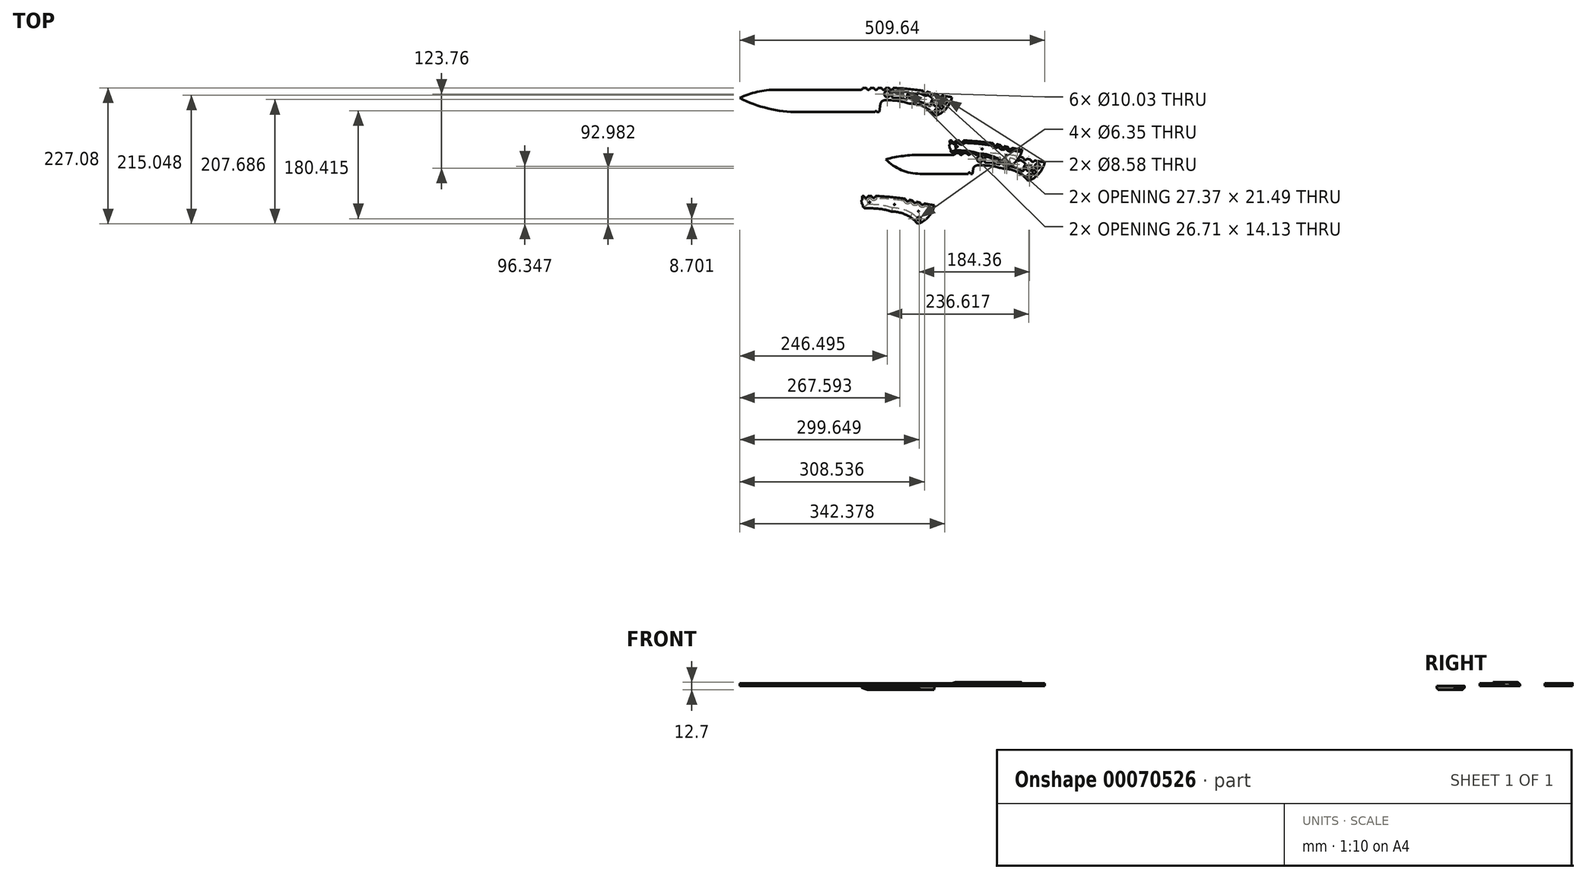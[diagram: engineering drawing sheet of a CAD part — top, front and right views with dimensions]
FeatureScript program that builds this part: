
annotation { "Feature Type Name" : "Feature", "Feature Type Description" : "" }
export const myFeature = defineFeature(function(context is Context, id is Id, definition is map)
    precondition{}
    {
        {
            var Q0;
            Q0=qCreatedBy(makeId("Top.planeOp"),FACE);
            var sketch = newSketch(context, id + "F0", { "sketchPlane" : qUnion([Q0])});
            skLineSegment(sketch, "E0", {"start": v(-84.54, 13.28) * mm, "end": v(-84.54, 13.28) * mm});
            skPoint(sketch, "E1", {"position": v(108.15, 3.1) * mm});
            skLineSegment(sketch, "E2", {"start": v(-12.95, 49.77) * mm, "end": v(-6.6, 49.77) * mm});
            skLineSegment(sketch, "E3", {"start": v(-0.25, 49.77) * mm, "end": v(6.1, 49.77) * mm});
            skLineSegment(sketch, "E4", {"start": v(-41.06, 46.66) * mm, "end": v(-70.9, 46.66) * mm});
            skPoint(sketch, "E5", {"position": v(-130.65, 40.32) * mm});
            skPoint(sketch, "E6", {"position": v(-84.54, 13.28) * mm});
            skLineSegment(sketch, "E7", {"start": v(15.4, 14.9) * mm, "end": v(-72, 14.9) * mm});
            skLineSegment(sketch, "E8", {"start": v(-41.06, 46.66) * mm, "end": v(-16.12, 46.66) * mm});
            skLineSegment(sketch, "E9", {"start": v(31.12, 29.1) * mm, "end": v(24.2, 29.1) * mm});
            skLineSegment(sketch, "E10", {"start": v(15.4, 14.9) * mm, "end": v(16.47, 23.28) * mm});
            skArc(sketch, "E11", {"start": v(24.2, 29.1) * mm, "mid": v(19.36, 27.48) * mm, "end": v(16.47, 23.28) * mm});
            skPoint(sketch, "E12", {"position": v(95.42, 14.98) * mm});
            skPoint(sketch, "E13", {"position": v(96.98, 42.66) * mm});
            skPoint(sketch, "E14", {"position": v(136.23, 34.28) * mm});
            skArc(sketch, "E15", {"start": v(83.35, 45.62) * mm, "mid": v(60.26, 48.23) * mm, "end": v(37.06, 49.73) * mm});
            skArc(sketch, "E16", {"start": v(96.98, 42.66) * mm, "mid": v(90.2, 44.33) * mm, "end": v(83.35, 45.62) * mm});
            skArc(sketch, "E17", {"start": v(96.98, 42.66) * mm, "mid": v(116.43, 37.68) * mm, "end": v(136.23, 34.28) * mm});
            skArc(sketch, "E18", {"start": v(64.66, 23.87) * mm, "mid": v(48.1, 27.78) * mm, "end": v(31.12, 29.1) * mm});
            skArc(sketch, "E19", {"start": v(108.15, 3.1) * mm, "mid": v(126.27, 15.01) * mm, "end": v(136.23, 34.28) * mm});
            skPoint(sketch, "E20", {"position": v(109.7, 24.2) * mm});
            skPoint(sketch, "E21", {"position": v(27.97, 39.43) * mm});
            skPoint(sketch, "E22", {"position": v(69.43, 35.5) * mm});
            skCircle(sketch, "E23", {"center": v(27.97, 39.43) * mm, "radius": 5.02 * mm});
            skCircle(sketch, "E24", {"center": v(69.43, 35.5) * mm, "radius": 5.02 * mm});
            skCircle(sketch, "E25", {"center": v(109.7, 24.2) * mm, "radius": 5.02 * mm});
            skLineSegment(sketch, "E26", {"start": v(49.3, 44.08) * mm, "end": v(39.93, 44.8) * mm});
            skPoint(sketch, "E27", {"position": v(38.2, 44.27) * mm});
            skPoint(sketch, "E28", {"position": v(36.72, 43.37) * mm});
            skPoint(sketch, "E29", {"position": v(36.71, 43.38) * mm});
            skPoint(sketch, "E30", {"position": v(36.14, 42.04) * mm});
            skLineSegment(sketch, "E31", {"start": v(60.01, 30.7) * mm, "end": v(48.1, 32.86) * mm});
            skLineSegment(sketch, "E32", {"start": v(49.3, 44.08) * mm, "end": v(61.08, 42.46) * mm});
            skArc(sketch, "E33", {"start": v(62.23, 40.16) * mm, "mid": v(62.26, 41.61) * mm, "end": v(61.08, 42.46) * mm});
            skArc(sketch, "E34", {"start": v(60.01, 30.7) * mm, "mid": v(61.2, 31.1) * mm, "end": v(61.46, 32.34) * mm});
            skPoint(sketch, "E35", {"position": v(101.38, 22.16) * mm});
            skArc(sketch, "E36", {"start": v(97.9, 19.97) * mm, "mid": v(88.55, 24.54) * mm, "end": v(78.52, 27.36) * mm});
            skArc(sketch, "E37", {"start": v(97.9, 19.97) * mm, "mid": v(100.33, 19.98) * mm, "end": v(101.38, 22.16) * mm});
            skArc(sketch, "E38", {"start": v(86.88, 38.6) * mm, "mid": v(83.15, 40.14) * mm, "end": v(79.22, 41.06) * mm});
            skArc(sketch, "E39", {"start": v(79.22, 41.06) * mm, "mid": v(77.66, 40.69) * mm, "end": v(77.18, 39.16) * mm});
            skArc(sketch, "E40", {"start": v(98.36, 36.23) * mm, "mid": v(96.56, 37.18) * mm, "end": v(94.53, 37.33) * mm});
            skArc(sketch, "E41", {"start": v(102.92, 29.44) * mm, "mid": v(103.7, 31.05) * mm, "end": v(102.92, 32.65) * mm});
            skArc(sketch, "E42", {"start": v(102.92, 29.44) * mm, "mid": v(101.33, 25.97) * mm, "end": v(101.38, 22.16) * mm});
            skArc(sketch, "E43", {"start": v(35.72, 35.78) * mm, "mid": v(36.45, 38.52) * mm, "end": v(36.31, 41.35) * mm});
            skArc(sketch, "E44", {"start": v(35.72, 35.78) * mm, "mid": v(36.05, 34.52) * mm, "end": v(37.13, 33.78) * mm});
            skLineSegment(sketch, "E45", {"start": v(37.13, 33.78) * mm, "end": v(48.1, 32.86) * mm});
            skArc(sketch, "E46", {"start": v(95.42, 14.98) * mm, "mid": v(80.62, 21.43) * mm, "end": v(64.66, 23.87) * mm});
            skArc(sketch, "E47", {"start": v(108.15, 3.1) * mm, "mid": v(102.33, 9.63) * mm, "end": v(95.42, 14.98) * mm});
            skLineSegment(sketch, "E48", {"start": v(108.15, 3.1) * mm, "end": v(108.15, 3.1) * mm});
            skArc(sketch, "E49", {"start": v(86.88, 38.6) * mm, "mid": v(90.58, 37.18) * mm, "end": v(94.53, 37.33) * mm});
            skLineSegment(sketch, "E50", {"start": v(98.36, 36.23) * mm, "end": v(102.92, 32.65) * mm});
            skArc(sketch, "E51", {"start": v(39.93, 44.8) * mm, "mid": v(37.35, 43.88) * mm, "end": v(36.31, 41.35) * mm});
            skArc(sketch, "E52", {"start": v(62.23, 40.16) * mm, "mid": v(61.06, 36.33) * mm, "end": v(61.46, 32.34) * mm});
            skArc(sketch, "E53", {"start": v(76.66, 31.15) * mm, "mid": v(76.58, 28.76) * mm, "end": v(78.52, 27.36) * mm});
            skArc(sketch, "E54", {"start": v(76.66, 31.15) * mm, "mid": v(77.84, 35.1) * mm, "end": v(77.18, 39.16) * mm});
            skCircle(sketch, "E55", {"center": v(123.85, 27.57) * mm, "radius": 4.3 * mm});
            skCircle(sketch, "E56", {"center": v(110.6, 11.8) * mm, "radius": 3.18 * mm});
            skCircle(sketch, "E57", {"center": v(118.5, 17.8) * mm, "radius": 2.9 * mm});
            skCircle(sketch, "E58", {"center": v(10.19, 14.9) * mm, "radius": 2.06 * mm});
            skArc(sketch, "E59", {"start": v(-129.4, 39) * mm, "mid": v(-103.12, 21.18) * mm, "end": v(-72, 14.9) * mm});
            skArc(sketch, "E60", {"start": v(-70.9, 46.66) * mm, "mid": v(-100.4, 44.74) * mm, "end": v(-129.4, 39) * mm});
            skArc(sketch, "E61", {"start": v(-16.12, 46.66) * mm, "mid": v(-13.9, 47.57) * mm, "end": v(-12.95, 49.77) * mm});
            skArc(sketch, "E62", {"start": v(-6.6, 49.77) * mm, "mid": v(-3.42, 46.58) * mm, "end": v(-0.25, 49.77) * mm});
            skArc(sketch, "E63", {"start": v(6.1, 49.77) * mm, "mid": v(9.28, 46.6) * mm, "end": v(12.45, 49.77) * mm});
            skLineSegment(sketch, "E64", {"start": v(12.45, 49.77) * mm, "end": v(18.8, 49.77) * mm});
            skArc(sketch, "E65", {"start": v(18.8, 49.77) * mm, "mid": v(21.98, 46.59) * mm, "end": v(25.15, 49.77) * mm});
            skArc(sketch, "E66", {"start": v(31.5, 49.77) * mm, "mid": v(34.64, 46.57) * mm, "end": v(37.86, 49.7) * mm});
            skLineSegment(sketch, "E67", {"start": v(25.15, 49.77) * mm, "end": v(31.5, 49.77) * mm});
            skLineSegment(sketch, "E68", {"start": v(24.2, 29.1) * mm, "end": v(16.9, 29.1) * mm});
            skLineSegment(sketch, "E69", {"start": v(15.3, 49.77) * mm, "end": v(15.84, 42.69) * mm});
            skLineSegment(sketch, "E70", {"start": v(15.84, 42.69) * mm, "end": v(14.33, 42.57) * mm});
            skLineSegment(sketch, "E71", {"start": v(16.9, 29.1) * mm, "end": v(16.34, 36.2) * mm});
            skLineSegment(sketch, "E72", {"start": v(16.34, 36.2) * mm, "end": v(14.83, 36.08) * mm});
            skLineSegment(sketch, "E73", {"start": v(14.83, 36.08) * mm, "end": v(14.33, 42.57) * mm});
            skLineSegment(sketch, "E74", {"start": v(15.3, 49.77) * mm, "end": v(18.8, 49.77) * mm});
            skArc(sketch, "E75", {"start": v(88.27, 44.74) * mm, "mid": v(90.66, 40.96) * mm, "end": v(94.46, 43.33) * mm});
            skArc(sketch, "E76", {"start": v(100.59, 41.6) * mm, "mid": v(102.9, 38.11) * mm, "end": v(106.67, 39.97) * mm});
            skArc(sketch, "E77", {"start": v(112.8, 38.48) * mm, "mid": v(115.41, 35.07) * mm, "end": v(119.18, 37.1) * mm});
            skSolve(sketch);
        }
        {
            var Q0;
            {var subQ13=sQuery(id+"F0.wireOp",EDGE,"E2");Q0=makeQuery(id+"F0.imprint","IMPRINT",FACE,{"disambiguationData":[TD([[makeQuery(id+"F0.imprint","IMPRINT",EDGE,{"derivedFrom":subQ13}),-1.0]])]});}
            var Q1;
            Q1=makeQuery(id+"F0.imprint","IMPRINT",FACE,{"disambiguationData":[TD([[makeQuery(id+"F0.imprint","IMPRINT",EDGE,{"derivedFrom":sQuery(id+"F0.wireOp",EDGE,"E9")}),-1.0]])]});
            extrude(context, id + "F1", {"entities" : qUnion([Q0, Q1]), "depth" : 4.75 * mm});
        }
        {
            var Q0;
            Q0=qCreatedBy(makeId("Top.planeOp"),FACE);
            var sketch = newSketch(context, id + "F2", { "sketchPlane" : qUnion([Q0])});
            skPoint(sketch, "E78", {"position": v(70.3, 23.95) * mm});
            skLineSegment(sketch, "E79", {"start": v(-6.72, 49.94) * mm, "end": v(-13.65, 49.94) * mm});
            skPoint(sketch, "E80", {"position": v(57.58, 35.82) * mm});
            skPoint(sketch, "E81", {"position": v(59.14, 63.5) * mm});
            skPoint(sketch, "E82", {"position": v(98.39, 55.12) * mm});
            skArc(sketch, "E83", {"start": v(45.52, 66.46) * mm, "mid": v(22.42, 69.08) * mm, "end": v(-0.78, 70.57) * mm});
            skArc(sketch, "E84", {"start": v(59.14, 63.5) * mm, "mid": v(52.37, 65.18) * mm, "end": v(45.52, 66.46) * mm});
            skArc(sketch, "E85", {"start": v(59.14, 63.5) * mm, "mid": v(78.6, 58.52) * mm, "end": v(98.39, 55.12) * mm});
            skArc(sketch, "E86", {"start": v(26.82, 44.7) * mm, "mid": v(10.25, 48.62) * mm, "end": v(-6.72, 49.94) * mm});
            skArc(sketch, "E87", {"start": v(70.3, 23.95) * mm, "mid": v(88.44, 35.85) * mm, "end": v(98.39, 55.12) * mm});
            skPoint(sketch, "E88", {"position": v(71.87, 45.04) * mm});
            skPoint(sketch, "E89", {"position": v(-9.87, 60.27) * mm});
            skPoint(sketch, "E90", {"position": v(31.6, 56.35) * mm});
            skCircle(sketch, "E91", {"center": v(-9.87, 60.27) * mm, "radius": 0.8 * mm});
            skCircle(sketch, "E92", {"center": v(31.6, 56.35) * mm, "radius": 0.8 * mm});
            skCircle(sketch, "E93", {"center": v(71.87, 45.04) * mm, "radius": 0.8 * mm});
            skPoint(sketch, "E94", {"position": v(63.54, 43) * mm});
            skArc(sketch, "E95", {"start": v(57.58, 35.82) * mm, "mid": v(42.78, 42.28) * mm, "end": v(26.82, 44.7) * mm});
            skArc(sketch, "E96", {"start": v(70.3, 23.95) * mm, "mid": v(64.5, 30.47) * mm, "end": v(57.58, 35.82) * mm});
            skLineSegment(sketch, "E97", {"start": v(70.3, 23.95) * mm, "end": v(70.3, 23.95) * mm});
            skCircle(sketch, "E98", {"center": v(72.76, 32.65) * mm, "radius": 3.18 * mm});
            skArc(sketch, "E99", {"start": v(-19.03, 70.61) * mm, "mid": v(-15.86, 67.43) * mm, "end": v(-12.68, 70.61) * mm});
            skArc(sketch, "E100", {"start": v(-6.33, 70.61) * mm, "mid": v(-3.2, 67.41) * mm, "end": v(0.02, 70.54) * mm});
            skLineSegment(sketch, "E101", {"start": v(-12.68, 70.61) * mm, "end": v(-6.33, 70.61) * mm});
            skLineSegment(sketch, "E102", {"start": v(-22.54, 70.61) * mm, "end": v(-22, 63.53) * mm});
            skLineSegment(sketch, "E103", {"start": v(-22, 63.53) * mm, "end": v(-23.51, 63.41) * mm});
            skLineSegment(sketch, "E104", {"start": v(-21.5, 57.04) * mm, "end": v(-23, 56.92) * mm});
            skLineSegment(sketch, "E105", {"start": v(-23, 56.92) * mm, "end": v(-23.51, 63.41) * mm});
            skLineSegment(sketch, "E106", {"start": v(-22.54, 70.61) * mm, "end": v(-19.03, 70.61) * mm});
            skArc(sketch, "E107", {"start": v(50.43, 65.58) * mm, "mid": v(52.83, 61.8) * mm, "end": v(56.62, 64.17) * mm});
            skArc(sketch, "E108", {"start": v(62.75, 62.45) * mm, "mid": v(65.07, 58.95) * mm, "end": v(68.83, 60.81) * mm});
            skArc(sketch, "E109", {"start": v(74.97, 59.32) * mm, "mid": v(77.57, 55.92) * mm, "end": v(81.35, 57.95) * mm});
            skArc(sketch, "E110", {"start": v(-18.95, 49.94) * mm, "mid": v(-19.6, 51.38) * mm, "end": v(-21.1, 51.92) * mm});
            skLineSegment(sketch, "E111", {"start": v(-21.5, 57.04) * mm, "end": v(-21.1, 51.92) * mm});
            skLineSegment(sketch, "E112", {"start": v(-18.95, 49.94) * mm, "end": v(-13.65, 49.94) * mm});
            skSolve(sketch);
        }
        {
            var Q0;
            Q0=makeQuery(id+"F2.imprint","IMPRINT",FACE,{"disambiguationData":[TD([[makeQuery(id+"F2.imprint","IMPRINT",EDGE,{"derivedFrom":sQuery(id+"F2.wireOp",EDGE,"E79")}),-1.0]])]});
            extrude(context, id + "F3", {"entities" : qUnion([Q0]), "depth" : 6.35 * mm});
        }
        {
            var Q0;
            Q0=makeQuery(id+"F3.opExtrude","CAP_EDGE",EDGE,{"disambiguationData":[OSD([sQuery(id+"F2.wireOp",EDGE,"E83")])],"isStart":false});
            var Q1;
            Q1=makeQuery(id+"F3.opExtrude","CAP_EDGE",EDGE,{"disambiguationData":[OSD([sQuery(id+"F2.wireOp",EDGE,"E101")])],"isStart":false});
            var Q2;
            Q2=makeQuery(id+"F3.opExtrude","CAP_EDGE",EDGE,{"disambiguationData":[OSD([sQuery(id+"F2.wireOp",EDGE,"E106")])],"isStart":false});
            var Q3;
            {var subQ0=sQuery(id+"F2.wireOp",EDGE,"E84");Q3=makeQuery(id+"F3.opExtrude","CAP_EDGE",EDGE,{"disambiguationData":[OSD([subQ0]),TDD([makeQuery(id+"F2.imprint","IMPRINT",EDGE,{"disambiguationData":[TD([[makeQuery(id+"F2.imprint","INTERSECT",VERTEX,{"derivedFrom":[sQuery(id+"F2.wireOp",EDGE,"E83"),subQ0]}),1.0]])],"derivedFrom":subQ0})])],"isStart":false});}
            var Q4;
            {var subQ0=sQuery(id+"F2.wireOp",EDGE,"E85");Q4=makeQuery(id+"F3.opExtrude","CAP_EDGE",EDGE,{"disambiguationData":[OSD([subQ0]),TDD([makeQuery(id+"F2.imprint","IMPRINT",EDGE,{"disambiguationData":[TD([[makeQuery(id+"F2.imprint","INTERSECT",VERTEX,{"derivedFrom":[sQuery(id+"F2.wireOp",EDGE,"E84"),subQ0]}),-1.0]])],"derivedFrom":subQ0})])],"isStart":false});}
            var Q5;
            {var subQ0=sQuery(id+"F2.wireOp",EDGE,"E84");Q5=makeQuery(id+"F3.opExtrude","CAP_EDGE",EDGE,{"disambiguationData":[OSD([subQ0]),TDD([makeQuery(id+"F2.imprint","IMPRINT",EDGE,{"disambiguationData":[TD([[makeQuery(id+"F2.imprint","INTERSECT",VERTEX,{"derivedFrom":[subQ0,sQuery(id+"F2.wireOp",EDGE,"E85")]}),-1.0]])],"derivedFrom":subQ0})])],"isStart":false});}
            var Q6;
            {var subQ0=sQuery(id+"F2.wireOp",EDGE,"E85");Q6=makeQuery(id+"F3.opExtrude","CAP_EDGE",EDGE,{"disambiguationData":[OSD([subQ0]),TDD([makeQuery(id+"F2.imprint","IMPRINT",EDGE,{"disambiguationData":[TD([[makeQuery(id+"F2.imprint","INTERSECT",VERTEX,{"disambiguationData":[OD(1.0)],"derivedFrom":[subQ0,sQuery(id+"F2.wireOp",EDGE,"E108")]}),-1.0]])],"derivedFrom":subQ0})])],"isStart":false});}
            var Q7;
            {var subQ0=sQuery(id+"F2.wireOp",EDGE,"E85");Q7=makeQuery(id+"F3.opExtrude","CAP_EDGE",EDGE,{"disambiguationData":[OSD([subQ0]),TDD([makeQuery(id+"F2.imprint","IMPRINT",EDGE,{"disambiguationData":[TD([[makeQuery(id+"F2.imprint","INTERSECT",VERTEX,{"derivedFrom":[subQ0,sQuery(id+"F2.wireOp",EDGE,"E87")]}),1.0]])],"derivedFrom":subQ0})])],"isStart":false});}
            var Q8;
            Q8=makeQuery(id+"F3.opExtrude","CAP_EDGE",EDGE,{"disambiguationData":[OSD([sQuery(id+"F2.wireOp",EDGE,"E109")])],"isStart":false});
            var Q9;
            Q9=makeQuery(id+"F3.opExtrude","CAP_EDGE",EDGE,{"disambiguationData":[OSD([sQuery(id+"F2.wireOp",EDGE,"E108")])],"isStart":false});
            var Q10;
            Q10=makeQuery(id+"F3.opExtrude","CAP_EDGE",EDGE,{"disambiguationData":[OSD([sQuery(id+"F2.wireOp",EDGE,"E107")])],"isStart":false});
            var Q11;
            Q11=makeQuery(id+"F3.opExtrude","CAP_EDGE",EDGE,{"disambiguationData":[OSD([sQuery(id+"F2.wireOp",EDGE,"E100")])],"isStart":false});
            var Q12;
            Q12=makeQuery(id+"F3.opExtrude","CAP_EDGE",EDGE,{"disambiguationData":[OSD([sQuery(id+"F2.wireOp",EDGE,"E99")])],"isStart":false});
            chamfer(context, id + "F4", {"entities" : qUnion([Q0, Q1, Q2, Q3, Q4, Q5, Q6, Q7, Q8, Q9, Q10, Q11, Q12]), "chamferType" : ChamferType.TWO_OFFSETS, "width1" : 3.8 * mm, "oppositeDirection" : false, "width2" : 3.8 * mm, "tangentPropagation" : true});
        }
        {
            var Q0;
            Q0=makeQuery(id+"F3.opExtrude","CAP_EDGE",EDGE,{"disambiguationData":[OSD([sQuery(id+"F2.wireOp",EDGE,"E79"),sQuery(id+"F2.wireOp",EDGE,"E112")])],"isStart":false});
            var Q1;
            Q1=makeQuery(id+"F3.opExtrude","CAP_EDGE",EDGE,{"disambiguationData":[OSD([sQuery(id+"F2.wireOp",EDGE,"E86")])],"isStart":false});
            var Q2;
            Q2=makeQuery(id+"F3.opExtrude","CAP_EDGE",EDGE,{"disambiguationData":[OSD([sQuery(id+"F2.wireOp",EDGE,"E95")])],"isStart":false});
            var Q3;
            Q3=makeQuery(id+"F3.opExtrude","CAP_EDGE",EDGE,{"disambiguationData":[OSD([sQuery(id+"F2.wireOp",EDGE,"E96")])],"isStart":false});
            chamfer(context, id + "F5", {"entities" : qUnion([Q0, Q1, Q2, Q3]), "chamferType" : ChamferType.TWO_OFFSETS, "width1" : 3.8 * mm, "oppositeDirection" : false, "width2" : 6.35 * mm, "tangentPropagation" : true});
        }
        {
            var Q0;
            Q0=makeQuery(id+"F3.opExtrude","CAP_EDGE",EDGE,{"disambiguationData":[OSD([sQuery(id+"F2.wireOp",EDGE,"E105")])],"isStart":false});
            chamfer(context, id + "F6", {"entities" : qUnion([Q0]), "chamferType" : ChamferType.TWO_OFFSETS, "width1" : 3.8 * mm, "oppositeDirection" : false, "width2" : 10.16 * mm});
        }
        {
            var Q0;
            Q0=qCreatedBy(makeId("Top.planeOp"),FACE);
            var sketch = newSketch(context, id + "F7", { "sketchPlane" : qUnion([Q0])});
            skPoint(sketch, "E113", {"position": v(-76.21, -68.78) * mm});
            skPoint(sketch, "E114", {"position": v(-76.22, -68.78) * mm});
            skLineSegment(sketch, "E115", {"start": v(-153.24, -42.8) * mm, "end": v(-160.17, -42.8) * mm});
            skPoint(sketch, "E116", {"position": v(-88.94, -56.9) * mm});
            skPoint(sketch, "E117", {"position": v(-87.38, -29.22) * mm});
            skPoint(sketch, "E118", {"position": v(-48.13, -37.6) * mm});
            skArc(sketch, "E119", {"start": v(-101, -26.27) * mm, "mid": v(-124.1, -23.65) * mm, "end": v(-147.3, -22.16) * mm});
            skArc(sketch, "E120", {"start": v(-87.38, -29.22) * mm, "mid": v(-94.15, -27.55) * mm, "end": v(-101, -26.27) * mm});
            skArc(sketch, "E121", {"start": v(-87.38, -29.22) * mm, "mid": v(-67.93, -34.2) * mm, "end": v(-48.13, -37.6) * mm});
            skArc(sketch, "E122", {"start": v(-119.7, -48.02) * mm, "mid": v(-136.27, -44.1) * mm, "end": v(-153.24, -42.8) * mm});
            skArc(sketch, "E123", {"start": v(-76.21, -68.78) * mm, "mid": v(-58.09, -56.87) * mm, "end": v(-48.13, -37.6) * mm});
            skPoint(sketch, "E124", {"position": v(-74.66, -47.68) * mm});
            skPoint(sketch, "E125", {"position": v(-156.39, -32.45) * mm});
            skPoint(sketch, "E126", {"position": v(-114.93, -36.38) * mm});
            skCircle(sketch, "E127", {"center": v(-156.39, -32.45) * mm, "radius": 0.8 * mm});
            skCircle(sketch, "E128", {"center": v(-114.93, -36.38) * mm, "radius": 0.8 * mm});
            skCircle(sketch, "E129", {"center": v(-74.66, -47.68) * mm, "radius": 0.8 * mm});
            skPoint(sketch, "E130", {"position": v(-82.98, -49.72) * mm});
            skArc(sketch, "E131", {"start": v(-88.94, -56.9) * mm, "mid": v(-103.74, -50.45) * mm, "end": v(-119.7, -48.02) * mm});
            skArc(sketch, "E132", {"start": v(-76.22, -68.78) * mm, "mid": v(-82.03, -62.25) * mm, "end": v(-88.94, -56.9) * mm});
            skLineSegment(sketch, "E133", {"start": v(-76.22, -68.78) * mm, "end": v(-76.21, -68.78) * mm});
            skCircle(sketch, "E134", {"center": v(-73.76, -60.08) * mm, "radius": 3.18 * mm});
            skArc(sketch, "E135", {"start": v(-165.55, -22.11) * mm, "mid": v(-162.38, -25.3) * mm, "end": v(-159.2, -22.11) * mm});
            skArc(sketch, "E136", {"start": v(-152.86, -22.11) * mm, "mid": v(-149.72, -25.31) * mm, "end": v(-146.5, -22.19) * mm});
            skLineSegment(sketch, "E137", {"start": v(-159.2, -22.11) * mm, "end": v(-152.86, -22.11) * mm});
            skLineSegment(sketch, "E138", {"start": v(-169.07, -22.11) * mm, "end": v(-168.52, -29.2) * mm});
            skLineSegment(sketch, "E139", {"start": v(-168.52, -29.2) * mm, "end": v(-170.04, -29.32) * mm});
            skLineSegment(sketch, "E140", {"start": v(-168.02, -35.69) * mm, "end": v(-169.53, -35.8) * mm});
            skLineSegment(sketch, "E141", {"start": v(-169.53, -35.8) * mm, "end": v(-170.04, -29.32) * mm});
            skLineSegment(sketch, "E142", {"start": v(-169.07, -22.11) * mm, "end": v(-165.55, -22.11) * mm});
            skArc(sketch, "E143", {"start": v(-96.1, -27.15) * mm, "mid": v(-93.7, -30.92) * mm, "end": v(-89.9, -28.55) * mm});
            skArc(sketch, "E144", {"start": v(-83.77, -30.28) * mm, "mid": v(-81.45, -33.77) * mm, "end": v(-77.69, -31.92) * mm});
            skArc(sketch, "E145", {"start": v(-71.55, -33.4) * mm, "mid": v(-68.95, -36.8) * mm, "end": v(-65.18, -34.78) * mm});
            skArc(sketch, "E146", {"start": v(-165.47, -42.8) * mm, "mid": v(-166.13, -41.35) * mm, "end": v(-167.62, -40.8) * mm});
            skLineSegment(sketch, "E147", {"start": v(-168.02, -35.69) * mm, "end": v(-167.62, -40.8) * mm});
            skLineSegment(sketch, "E148", {"start": v(-165.47, -42.8) * mm, "end": v(-160.17, -42.8) * mm});
            skSolve(sketch);
        }
        {
            var Q0;
            Q0=makeQuery(id+"F7.imprint","IMPRINT",FACE,{"disambiguationData":[TD([[makeQuery(id+"F7.imprint","IMPRINT",EDGE,{"derivedFrom":sQuery(id+"F7.wireOp",EDGE,"E115")}),-1.0]])]});
            extrude(context, id + "F8", {"entities" : qUnion([Q0]), "oppositeDirection" : true, "depth" : 6.35 * mm});
        }
        {
            var Q0;
            Q0=makeQuery(id+"F8.opExtrude","CAP_EDGE",EDGE,{"disambiguationData":[OSD([sQuery(id+"F7.wireOp",EDGE,"E142")])],"isStart":false});
            var Q1;
            Q1=makeQuery(id+"F8.opExtrude","CAP_EDGE",EDGE,{"disambiguationData":[OSD([sQuery(id+"F7.wireOp",EDGE,"E137")])],"isStart":false});
            var Q2;
            Q2=makeQuery(id+"F8.opExtrude","CAP_EDGE",EDGE,{"disambiguationData":[OSD([sQuery(id+"F7.wireOp",EDGE,"E119")])],"isStart":false});
            var Q3;
            {var subQ0=sQuery(id+"F7.wireOp",EDGE,"E120");Q3=makeQuery(id+"F8.opExtrude","CAP_EDGE",EDGE,{"disambiguationData":[OSD([subQ0]),TDD([makeQuery(id+"F7.imprint","IMPRINT",EDGE,{"disambiguationData":[TD([[makeQuery(id+"F7.imprint","INTERSECT",VERTEX,{"derivedFrom":[sQuery(id+"F7.wireOp",EDGE,"E119"),subQ0]}),1.0]])],"derivedFrom":subQ0})])],"isStart":false});}
            var Q4;
            {var subQ0=sQuery(id+"F7.wireOp",EDGE,"E121");Q4=makeQuery(id+"F8.opExtrude","CAP_EDGE",EDGE,{"disambiguationData":[OSD([subQ0]),TDD([makeQuery(id+"F7.imprint","IMPRINT",EDGE,{"disambiguationData":[TD([[makeQuery(id+"F7.imprint","INTERSECT",VERTEX,{"derivedFrom":[sQuery(id+"F7.wireOp",EDGE,"E120"),subQ0]}),-1.0]])],"derivedFrom":subQ0})])],"isStart":false});}
            var Q5;
            {var subQ0=sQuery(id+"F7.wireOp",EDGE,"E120");Q5=makeQuery(id+"F8.opExtrude","CAP_EDGE",EDGE,{"disambiguationData":[OSD([subQ0]),TDD([makeQuery(id+"F7.imprint","IMPRINT",EDGE,{"disambiguationData":[TD([[makeQuery(id+"F7.imprint","INTERSECT",VERTEX,{"derivedFrom":[subQ0,sQuery(id+"F7.wireOp",EDGE,"E121")]}),-1.0]])],"derivedFrom":subQ0})])],"isStart":false});}
            var Q6;
            {var subQ0=sQuery(id+"F7.wireOp",EDGE,"E121");Q6=makeQuery(id+"F8.opExtrude","CAP_EDGE",EDGE,{"disambiguationData":[OSD([subQ0]),TDD([makeQuery(id+"F7.imprint","IMPRINT",EDGE,{"disambiguationData":[TD([[makeQuery(id+"F7.imprint","INTERSECT",VERTEX,{"disambiguationData":[OD(1.0)],"derivedFrom":[subQ0,sQuery(id+"F7.wireOp",EDGE,"E144")]}),-1.0]])],"derivedFrom":subQ0})])],"isStart":false});}
            var Q7;
            {var subQ0=sQuery(id+"F7.wireOp",EDGE,"E121");Q7=makeQuery(id+"F8.opExtrude","CAP_EDGE",EDGE,{"disambiguationData":[OSD([subQ0]),TDD([makeQuery(id+"F7.imprint","IMPRINT",EDGE,{"disambiguationData":[TD([[makeQuery(id+"F7.imprint","INTERSECT",VERTEX,{"derivedFrom":[subQ0,sQuery(id+"F7.wireOp",EDGE,"E123")]}),1.0]])],"derivedFrom":subQ0})])],"isStart":false});}
            var Q8;
            Q8=makeQuery(id+"F8.opExtrude","CAP_EDGE",EDGE,{"disambiguationData":[OSD([sQuery(id+"F7.wireOp",EDGE,"E145")])],"isStart":false});
            var Q9;
            Q9=makeQuery(id+"F8.opExtrude","CAP_EDGE",EDGE,{"disambiguationData":[OSD([sQuery(id+"F7.wireOp",EDGE,"E144")])],"isStart":false});
            var Q10;
            Q10=makeQuery(id+"F8.opExtrude","CAP_EDGE",EDGE,{"disambiguationData":[OSD([sQuery(id+"F7.wireOp",EDGE,"E143")])],"isStart":false});
            var Q11;
            Q11=makeQuery(id+"F8.opExtrude","CAP_EDGE",EDGE,{"disambiguationData":[OSD([sQuery(id+"F7.wireOp",EDGE,"E136")])],"isStart":false});
            var Q12;
            Q12=makeQuery(id+"F8.opExtrude","CAP_EDGE",EDGE,{"disambiguationData":[OSD([sQuery(id+"F7.wireOp",EDGE,"E135")])],"isStart":false});
            chamfer(context, id + "F9", {"entities" : qUnion([Q0, Q1, Q2, Q3, Q4, Q5, Q6, Q7, Q8, Q9, Q10, Q11, Q12]), "chamferType" : ChamferType.TWO_OFFSETS, "width1" : 3.8 * mm, "oppositeDirection" : false, "width2" : 3.8 * mm, "tangentPropagation" : true});
        }
        {
            var Q0;
            Q0=makeQuery(id+"F8.opExtrude","CAP_EDGE",EDGE,{"disambiguationData":[OSD([sQuery(id+"F7.wireOp",EDGE,"E122")])],"isStart":false});
            var Q1;
            Q1=makeQuery(id+"F8.opExtrude","CAP_EDGE",EDGE,{"disambiguationData":[OSD([sQuery(id+"F7.wireOp",EDGE,"E115"),sQuery(id+"F7.wireOp",EDGE,"E148")])],"isStart":false});
            var Q2;
            Q2=makeQuery(id+"F8.opExtrude","CAP_EDGE",EDGE,{"disambiguationData":[OSD([sQuery(id+"F7.wireOp",EDGE,"E131")])],"isStart":false});
            var Q3;
            Q3=makeQuery(id+"F8.opExtrude","CAP_EDGE",EDGE,{"disambiguationData":[OSD([sQuery(id+"F7.wireOp",EDGE,"E132")])],"isStart":false});
            chamfer(context, id + "F10", {"entities" : qUnion([Q0, Q1, Q2, Q3]), "chamferType" : ChamferType.TWO_OFFSETS, "width1" : 6.35 * mm, "oppositeDirection" : false, "width2" : 3.8 * mm, "tangentPropagation" : true});
        }
        {
            var Q0;
            Q0=makeQuery(id+"F8.opExtrude","CAP_EDGE",EDGE,{"disambiguationData":[OSD([sQuery(id+"F7.wireOp",EDGE,"E141")])],"isStart":false});
            chamfer(context, id + "F11", {"entities" : qUnion([Q0]), "chamferType" : ChamferType.TWO_OFFSETS, "width1" : 10.16 * mm, "oppositeDirection" : false, "width2" : 3.8 * mm, "tangentPropagation" : true});
        }
        {
            var Q0;
            Q0=qCreatedBy(makeId("Top.planeOp"),FACE);
            var sketch = newSketch(context, id + "F12", { "sketchPlane" : qUnion([Q0])});
            skLineSegment(sketch, "E149", {"start": v(-239.43, 121.81) * mm, "end": v(-239.43, 121.81) * mm});
            skPoint(sketch, "E150", {"position": v(-46.74, 111.64) * mm});
            skLineSegment(sketch, "E151", {"start": v(-167.83, 158.3) * mm, "end": v(-161.48, 158.3) * mm});
            skLineSegment(sketch, "E152", {"start": v(-155.13, 158.3) * mm, "end": v(-148.78, 158.3) * mm});
            skLineSegment(sketch, "E153", {"start": v(-195.95, 155.19) * mm, "end": v(-225.78, 155.19) * mm});
            skPoint(sketch, "E154", {"position": v(-285.53, 148.85) * mm});
            skPoint(sketch, "E155", {"position": v(-239.43, 121.81) * mm});
            skLineSegment(sketch, "E156", {"start": v(-195.95, 155.19) * mm, "end": v(-171, 155.19) * mm});
            skLineSegment(sketch, "E157", {"start": v(-123.77, 137.62) * mm, "end": v(-130.7, 137.62) * mm});
            skLineSegment(sketch, "E158", {"start": v(-139.5, 123.44) * mm, "end": v(-138.41, 131.8) * mm});
            skArc(sketch, "E159", {"start": v(-130.7, 137.62) * mm, "mid": v(-135.53, 136) * mm, "end": v(-138.41, 131.8) * mm});
            skPoint(sketch, "E160", {"position": v(-59.47, 123.5) * mm});
            skPoint(sketch, "E161", {"position": v(-57.91, 151.2) * mm});
            skPoint(sketch, "E162", {"position": v(-18.66, 142.8) * mm});
            skArc(sketch, "E163", {"start": v(-71.53, 154.15) * mm, "mid": v(-94.63, 156.76) * mm, "end": v(-117.83, 158.26) * mm});
            skArc(sketch, "E164", {"start": v(-57.91, 151.2) * mm, "mid": v(-64.68, 152.86) * mm, "end": v(-71.53, 154.15) * mm});
            skArc(sketch, "E165", {"start": v(-57.91, 151.2) * mm, "mid": v(-38.45, 146.2) * mm, "end": v(-18.66, 142.8) * mm});
            skArc(sketch, "E166", {"start": v(-90.23, 132.4) * mm, "mid": v(-106.8, 136.3) * mm, "end": v(-123.77, 137.62) * mm});
            skArc(sketch, "E167", {"start": v(-46.74, 111.64) * mm, "mid": v(-28.61, 123.54) * mm, "end": v(-18.66, 142.8) * mm});
            skPoint(sketch, "E168", {"position": v(-45.18, 132.73) * mm});
            skPoint(sketch, "E169", {"position": v(-126.92, 147.96) * mm});
            skPoint(sketch, "E170", {"position": v(-85.46, 144.04) * mm});
            skCircle(sketch, "E171", {"center": v(-126.92, 147.96) * mm, "radius": 5.02 * mm});
            skCircle(sketch, "E172", {"center": v(-85.46, 144.04) * mm, "radius": 5.02 * mm});
            skCircle(sketch, "E173", {"center": v(-45.18, 132.73) * mm, "radius": 5.02 * mm});
            skLineSegment(sketch, "E174", {"start": v(-105.59, 152.6) * mm, "end": v(-114.96, 153.33) * mm});
            skPoint(sketch, "E175", {"position": v(-116.7, 152.8) * mm});
            skPoint(sketch, "E176", {"position": v(-118.17, 151.9) * mm});
            skPoint(sketch, "E177", {"position": v(-118.75, 150.57) * mm});
            skLineSegment(sketch, "E178", {"start": v(-94.88, 139.22) * mm, "end": v(-106.8, 141.39) * mm});
            skLineSegment(sketch, "E179", {"start": v(-105.59, 152.6) * mm, "end": v(-93.81, 151) * mm});
            skArc(sketch, "E180", {"start": v(-92.66, 148.69) * mm, "mid": v(-92.63, 150.14) * mm, "end": v(-93.81, 151) * mm});
            skArc(sketch, "E181", {"start": v(-94.88, 139.22) * mm, "mid": v(-93.68, 139.64) * mm, "end": v(-93.43, 140.87) * mm});
            skPoint(sketch, "E182", {"position": v(-53.51, 130.7) * mm});
            skArc(sketch, "E183", {"start": v(-56.98, 128.5) * mm, "mid": v(-66.34, 133.07) * mm, "end": v(-76.37, 135.9) * mm});
            skArc(sketch, "E184", {"start": v(-56.98, 128.5) * mm, "mid": v(-54.56, 128.51) * mm, "end": v(-53.51, 130.7) * mm});
            skArc(sketch, "E185", {"start": v(-68, 147.13) * mm, "mid": v(-71.74, 148.67) * mm, "end": v(-75.67, 149.59) * mm});
            skArc(sketch, "E186", {"start": v(-75.67, 149.59) * mm, "mid": v(-77.23, 149.22) * mm, "end": v(-77.7, 147.69) * mm});
            skArc(sketch, "E187", {"start": v(-56.52, 144.76) * mm, "mid": v(-58.32, 145.72) * mm, "end": v(-60.35, 145.86) * mm});
            skArc(sketch, "E188", {"start": v(-51.97, 137.97) * mm, "mid": v(-51.19, 139.58) * mm, "end": v(-51.97, 141.18) * mm});
            skArc(sketch, "E189", {"start": v(-51.97, 137.97) * mm, "mid": v(-53.55, 134.5) * mm, "end": v(-53.51, 130.7) * mm});
            skArc(sketch, "E190", {"start": v(-119.17, 144.3) * mm, "mid": v(-118.44, 147.05) * mm, "end": v(-118.57, 149.88) * mm});
            skArc(sketch, "E191", {"start": v(-119.17, 144.3) * mm, "mid": v(-118.84, 143.05) * mm, "end": v(-117.76, 142.31) * mm});
            skLineSegment(sketch, "E192", {"start": v(-117.76, 142.31) * mm, "end": v(-106.8, 141.39) * mm});
            skArc(sketch, "E193", {"start": v(-59.47, 123.5) * mm, "mid": v(-74.27, 129.96) * mm, "end": v(-90.23, 132.4) * mm});
            skArc(sketch, "E194", {"start": v(-46.74, 111.64) * mm, "mid": v(-52.56, 118.16) * mm, "end": v(-59.47, 123.5) * mm});
            skLineSegment(sketch, "E195", {"start": v(-46.74, 111.64) * mm, "end": v(-46.74, 111.64) * mm});
            skArc(sketch, "E196", {"start": v(-68, 147.13) * mm, "mid": v(-64.3, 145.71) * mm, "end": v(-60.35, 145.86) * mm});
            skLineSegment(sketch, "E197", {"start": v(-56.52, 144.76) * mm, "end": v(-51.97, 141.18) * mm});
            skArc(sketch, "E198", {"start": v(-114.96, 153.33) * mm, "mid": v(-117.53, 152.41) * mm, "end": v(-118.57, 149.88) * mm});
            skArc(sketch, "E199", {"start": v(-92.66, 148.69) * mm, "mid": v(-93.83, 144.86) * mm, "end": v(-93.43, 140.87) * mm});
            skArc(sketch, "E200", {"start": v(-78.22, 139.68) * mm, "mid": v(-78.3, 137.3) * mm, "end": v(-76.37, 135.9) * mm});
            skArc(sketch, "E201", {"start": v(-78.22, 139.68) * mm, "mid": v(-77.05, 143.63) * mm, "end": v(-77.7, 147.69) * mm});
            skCircle(sketch, "E202", {"center": v(-31.03, 136.1) * mm, "radius": 4.3 * mm});
            skCircle(sketch, "E203", {"center": v(-44.29, 120.34) * mm, "radius": 3.18 * mm});
            skCircle(sketch, "E204", {"center": v(-36.4, 126.33) * mm, "radius": 2.9 * mm});
            skArc(sketch, "E205", {"start": v(-171, 155.19) * mm, "mid": v(-168.78, 156.1) * mm, "end": v(-167.83, 158.3) * mm});
            skArc(sketch, "E206", {"start": v(-161.48, 158.3) * mm, "mid": v(-158.3, 155.12) * mm, "end": v(-155.13, 158.3) * mm});
            skArc(sketch, "E207", {"start": v(-148.78, 158.3) * mm, "mid": v(-145.6, 155.13) * mm, "end": v(-142.43, 158.3) * mm});
            skLineSegment(sketch, "E208", {"start": v(-142.43, 158.3) * mm, "end": v(-136.08, 158.3) * mm});
            skArc(sketch, "E209", {"start": v(-136.08, 158.3) * mm, "mid": v(-132.9, 155.12) * mm, "end": v(-129.73, 158.3) * mm});
            skArc(sketch, "E210", {"start": v(-123.38, 158.3) * mm, "mid": v(-120.24, 155.1) * mm, "end": v(-117.03, 158.22) * mm});
            skLineSegment(sketch, "E211", {"start": v(-129.73, 158.3) * mm, "end": v(-123.38, 158.3) * mm});
            skLineSegment(sketch, "E212", {"start": v(-139.6, 158.3) * mm, "end": v(-136.08, 158.3) * mm});
            skArc(sketch, "E213", {"start": v(-66.62, 153.27) * mm, "mid": v(-64.22, 149.5) * mm, "end": v(-60.43, 151.86) * mm});
            skArc(sketch, "E214", {"start": v(-54.3, 150.14) * mm, "mid": v(-51.98, 146.64) * mm, "end": v(-48.22, 148.5) * mm});
            skArc(sketch, "E215", {"start": v(-42.08, 147.01) * mm, "mid": v(-39.48, 143.6) * mm, "end": v(-35.7, 145.64) * mm});
            skLineSegment(sketch, "E216", {"start": v(-139.5, 123.44) * mm, "end": v(-140.2, 117.97) * mm});
            skArc(sketch, "E217", {"start": v(-373.41, 141.55) * mm, "mid": v(-325.81, 123.95) * mm, "end": v(-275.41, 117.97) * mm});
            skArc(sketch, "E218", {"start": v(-312.88, 155.19) * mm, "mid": v(-343.9, 151.69) * mm, "end": v(-373.41, 141.55) * mm});
            skLineSegment(sketch, "E219", {"start": v(-312.88, 155.19) * mm, "end": v(-225.78, 155.19) * mm});
            skLineSegment(sketch, "E220", {"start": v(-140.2, 117.97) * mm, "end": v(-144.23, 117.97) * mm});
            skArc(sketch, "E221", {"start": v(-144.23, 117.97) * mm, "mid": v(-145.87, 119.4) * mm, "end": v(-147.52, 117.97) * mm});
            skLineSegment(sketch, "E222", {"start": v(-147.52, 117.97) * mm, "end": v(-275.41, 117.97) * mm});
            skSolve(sketch);
        }
        {
            var Q0;
            Q0=makeQuery(id+"F12.imprint","IMPRINT",FACE,{"disambiguationData":[TD([[makeQuery(id+"F12.imprint","IMPRINT",EDGE,{"derivedFrom":sQuery(id+"F12.wireOp",EDGE,"E151")}),-1.0]])]});
            var Q1;
            Q1=makeQuery(id+"F12.imprint","IMPRINT",FACE,{"disambiguationData":[TD([[makeQuery(id+"F12.imprint","IMPRINT",EDGE,{"derivedFrom":sQuery(id+"F12.wireOp",EDGE,"E151")}),-1.0]])]});
            extrude(context, id + "F13", {"entities" : qUnion([Q0, Q1]), "depth" : 4.75 * mm});
        }
    });
